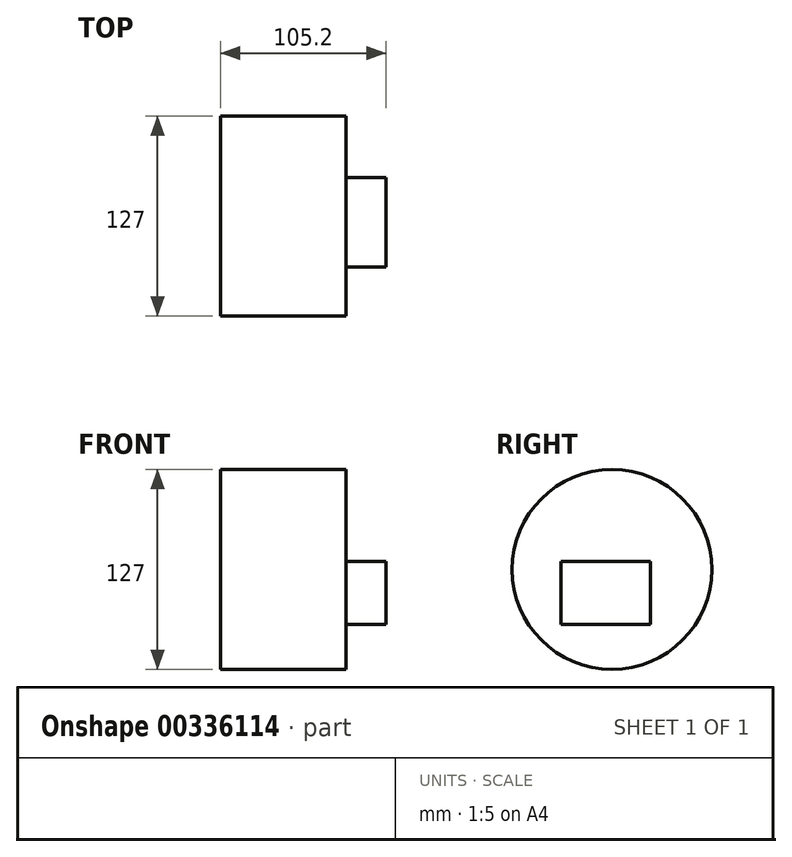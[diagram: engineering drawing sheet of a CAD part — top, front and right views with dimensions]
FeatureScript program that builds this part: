
annotation { "Feature Type Name" : "Feature", "Feature Type Description" : "" }
export const myFeature = defineFeature(function(context is Context, id is Id, definition is map)
    precondition{}
    {
        {
            var Q0;
            Q0=qCreatedBy(makeId("Right.planeOp"),FACE);
            var sketch = newSketch(context, id + "F0", { "sketchPlane" : qUnion([Q0])});
            skCircle(sketch, "E0", {"center": v(-24.45, 23.34) * mm, "radius": 63.5 * mm});
            skSolve(sketch);
        }
        {
            var Q0;
            Q0=makeQuery(id+"F0.imprint","IMPRINT",FACE,{"disambiguationData":[TD([[makeQuery(id+"F0.imprint","IMPRINT",EDGE,{"derivedFrom":sQuery(id+"F0.wireOp",EDGE,"E0")}),1.0]])]});
            extrude(context, id + "F1", {"entities" : qUnion([Q0]), "depth" : 79.8 * mm});
        }
        {
            var Q0;
            Q0=makeQuery(id+"F1.opExtrude","CAP_FACE",FACE,{"disambiguationData":[OSD([sQuery(id+"F0.wireOp",EDGE,"E0")])],"isStart":false});
            var sketch = newSketch(context, id + "F2", { "sketchPlane" : qUnion([Q0])});
            skLineSegment(sketch, "E1.bottom", {"start": v(-56.88, 28.58) * mm, "end": v(0, 28.58) * mm});
            skLineSegment(sketch, "E1.top", {"start": v(-56.88, -11.55) * mm, "end": v(0, -11.55) * mm});
            skLineSegment(sketch, "E1.left", {"start": v(-56.88, 28.58) * mm, "end": v(-56.88, -11.55) * mm});
            skLineSegment(sketch, "E1.right", {"start": v(0, 28.58) * mm, "end": v(0, -11.55) * mm});
            skLineSegment(sketch, "E2.bottom", {"start": v(0.71, -12) * mm, "end": v(0, -12) * mm});
            skLineSegment(sketch, "E2.top", {"start": v(0.71, 8.52) * mm, "end": v(0, 8.52) * mm});
            skLineSegment(sketch, "E2.left", {"start": v(0.71, -12) * mm, "end": v(0.71, 8.52) * mm});
            skLineSegment(sketch, "E2.right", {"start": v(0, -12) * mm, "end": v(0, 8.52) * mm});
            skSolve(sketch);
        }
        {
            var Q0;
            Q0=makeQuery(id+"F2.imprint","IMPRINT",FACE,{"disambiguationData":[TD([[makeQuery(id+"F2.imprint","IMPRINT",EDGE,{"derivedFrom":sQuery(id+"F2.wireOp",EDGE,"E1.bottom")}),-1.0]])]});
            extrude(context, id + "F3", {"entities" : qUnion([Q0]), "operationType" : NewBodyOperationType.ADD, "oppositeDirection" : true, "depth" : 40.9 * mm});
        }
        {
            var Q0;
            Q0=makeQuery(id+"F2.imprint","IMPRINT",FACE,{"disambiguationData":[TD([[makeQuery(id+"F2.imprint","IMPRINT",EDGE,{"derivedFrom":sQuery(id+"F2.wireOp",EDGE,"E1.bottom")}),-1.0]])]});
            extrude(context, id + "F4", {"entities" : qUnion([Q0]), "operationType" : NewBodyOperationType.ADD, "depth" : 25.4 * mm});
        }
    });
